# Revit family: Faucet_Touchless-Lavatory-KOHLER-Loure-K-28577T_1
name_source: partatom
category: Plumbing Fixtures
units: mm (PartAtom-declared; Revit-internal decimal feet)

## family parameters
Cut with Voids When Loaded = No
Host = Face
OmniClass Number = 23.31.11.00
OmniClass Title = Faucets
Part Type = Normal
Room Calculation Point = No
Round Connector Dimension = Use Diameter
Shared = No

## types (3) — shared parameters
ADA Compliant = No
Apparent Load = 0 VA
Assembly Code = D2010
CW Connection = Yes
Cold Water Inlet = Cold Water Inlet
Date Modified = 12/13/2022
Default Elevation = 36"
Drain Included = Yes
Electrical Connector = Yes
Electrical Note = One Dedicated Circuit Required
Faucet Hole Spacing = 0"
Finish = Kohler-Metal-CP-Polished_Chrome
HW Connection = No
Handle Clearance = 0"
Height = 14 7/16"
Hot Water Inlet = Hot Water Inlet
Length = 5 1/16"
Manufacturer = Kohler Co.
Master Format 2014 = 22 41 39
Master Format 2014 Name = Residential Faucets, Supplies, and Trim
Material = Brass Construction
Pressure = 43.00 psi
Product Name = Loure
Spout Reach = 5 1/16"
URL = http://www.kohler.com.cn
Vent Connection = No
Voltage = 220 V
Waste Connection = No
Waste Water Outlet = Waste Water Outlet
WaterSense Certified = No
Width = 2 7/16"

## per-type parameters (varying)
| type | Description | Flow Rate | Model | Product Documentation Link | Product Page URL | Type |
| 0.35 GPM, S3, CP-Polished Chrome | Lori Bowl Sensor Faucet (Single Cool, AC, Without Power Box 0.35GPM) | 0 GPM | K-28577T-S3-CP | https://files.kohler.com.cn | https://www.kohler.com.cn | 1 |
| 0.5 GPM, CP-Polished Chrome | Lori Bowl Sensor Faucet (Single Cool, AC, Without Power Box, 0.5GPM) | 1 GPM | K-28577T-CP | https://files.kohler.com.cn | https://www.kohler.com.cn | 2 |
| 0.5 GPM, NW, CP-Polished Chrome | Touchless Sensor Faucet Cold 0.5 GPM | 1 GPM | K-28577T-NW-CP |  |  | 3 |

## geometry (parser evidence)
native form markers: Sweep x6
no freeform markers — native parametric forms only
